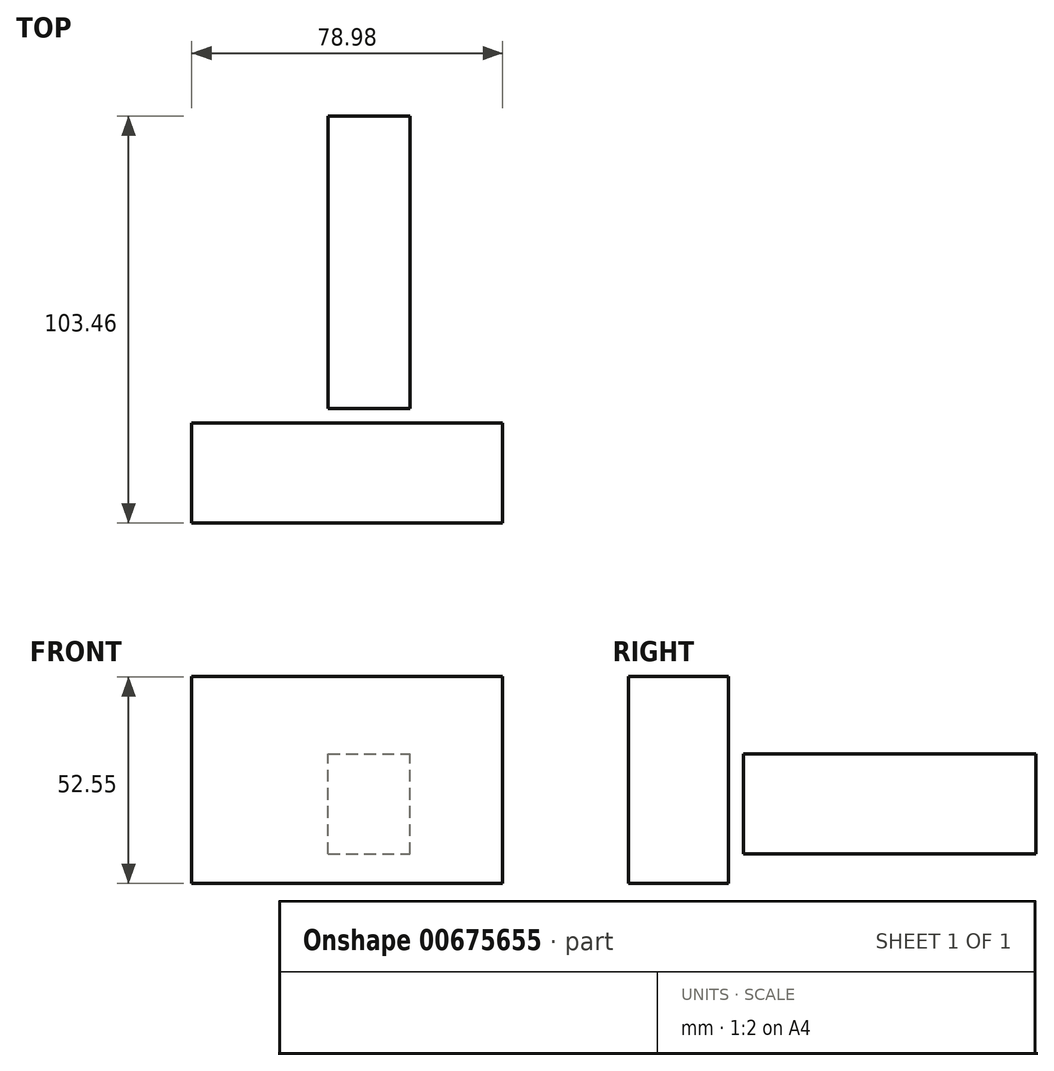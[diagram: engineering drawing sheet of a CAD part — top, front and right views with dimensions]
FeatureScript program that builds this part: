
annotation { "Feature Type Name" : "Feature", "Feature Type Description" : "" }
export const myFeature = defineFeature(function(context is Context, id is Id, definition is map)
    precondition{}
    {
        {
            var Q0;
            Q0=qCreatedBy(makeId("Front.planeOp"),FACE);
            var sketch = newSketch(context, id + "F0", { "sketchPlane" : qUnion([Q0])});
            skLineSegment(sketch, "E0.bottom", {"start": v(-41.84, 19.67) * mm, "end": v(37.14, 19.67) * mm});
            skLineSegment(sketch, "E0.top", {"start": v(-41.84, -32.88) * mm, "end": v(37.14, -32.88) * mm});
            skLineSegment(sketch, "E0.left", {"start": v(-41.84, 19.67) * mm, "end": v(-41.84, -32.88) * mm});
            skLineSegment(sketch, "E0.right", {"start": v(37.14, 19.67) * mm, "end": v(37.14, -32.88) * mm});
            skSolve(sketch);
        }
        {
            var Q0;
            Q0 = qSketchRegion(id + "F0", true);
            extrude(context, id + "F1", {"entities" : qUnion([Q0]), "depth" : 25.4 * mm, "offsetDistance" : 25.4 * mm});
        }
        {
            var Q0;
            Q0=qCreatedBy(makeId("Top.planeOp"),FACE);
            var sketch = newSketch(context, id + "F2", { "sketchPlane" : qUnion([Q0])});
            skLineSegment(sketch, "E1.bottom", {"start": v(-7.2, 3.74) * mm, "end": v(13.65, 3.74) * mm});
            skLineSegment(sketch, "E1.top", {"start": v(-7.2, 78.06) * mm, "end": v(13.65, 78.06) * mm});
            skLineSegment(sketch, "E1.left", {"start": v(-7.2, 3.74) * mm, "end": v(-7.2, 78.06) * mm});
            skLineSegment(sketch, "E1.right", {"start": v(13.65, 3.74) * mm, "end": v(13.65, 78.06) * mm});
            skSolve(sketch);
        }
        {
            var Q0;
            Q0 = qSketchRegion(id + "F2", true);
            extrude(context, id + "F3", {"entities" : qUnion([Q0]), "oppositeDirection" : true, "depth" : 25.4 * mm, "offsetDistance" : 25.4 * mm});
        }
    });
